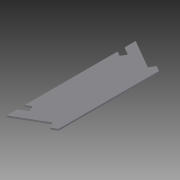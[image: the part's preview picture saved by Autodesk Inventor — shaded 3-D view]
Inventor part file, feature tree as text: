
AUTODESK INVENTOR PART (.ipt)
format: ipt  version: 2015 (Build 190159000, 159)  size: 113,664 bytes
history: native  units: in
note: dims shown in document units (in); Inventor stores cm internally (conversion verified against a paired STEP export)
features: reference x4, extrude x2, sketch x2
ambient origin geometry x8: Origin, YZ Plane, XZ Plane, XY Plane, X Axis, Y Axis, Z Axis, Center Point
bodies: Solid1 (feature_tree)
feature tree (8):
  extrude  "Extrusion1"  TaperAngle=30.0deg  [1 undecoded]
  extrude  "Extrusion2"  Depth=0.25in TaperAngle=0.0deg
  sketch  "Sketch1"  dims[d0=120.0deg d1=30.0deg]
  sketch  "Sketch3"  dims[d2=16.0in d3=0.25in d4=0.0in d5=6.0in d6=0.02in d7=0.02in d8=0.02in d9=0.02in d10=0.0in d11=0.0in]
  reference  "Reference5"
  reference  "Reference6"
  reference  "Reference7"
  reference  "Reference8"
note: 1 required parameter value undecoded (feature->parameter linkage not recoverable at this tier; creation-order binding heuristic only, values carry confidence <= 0.55)
